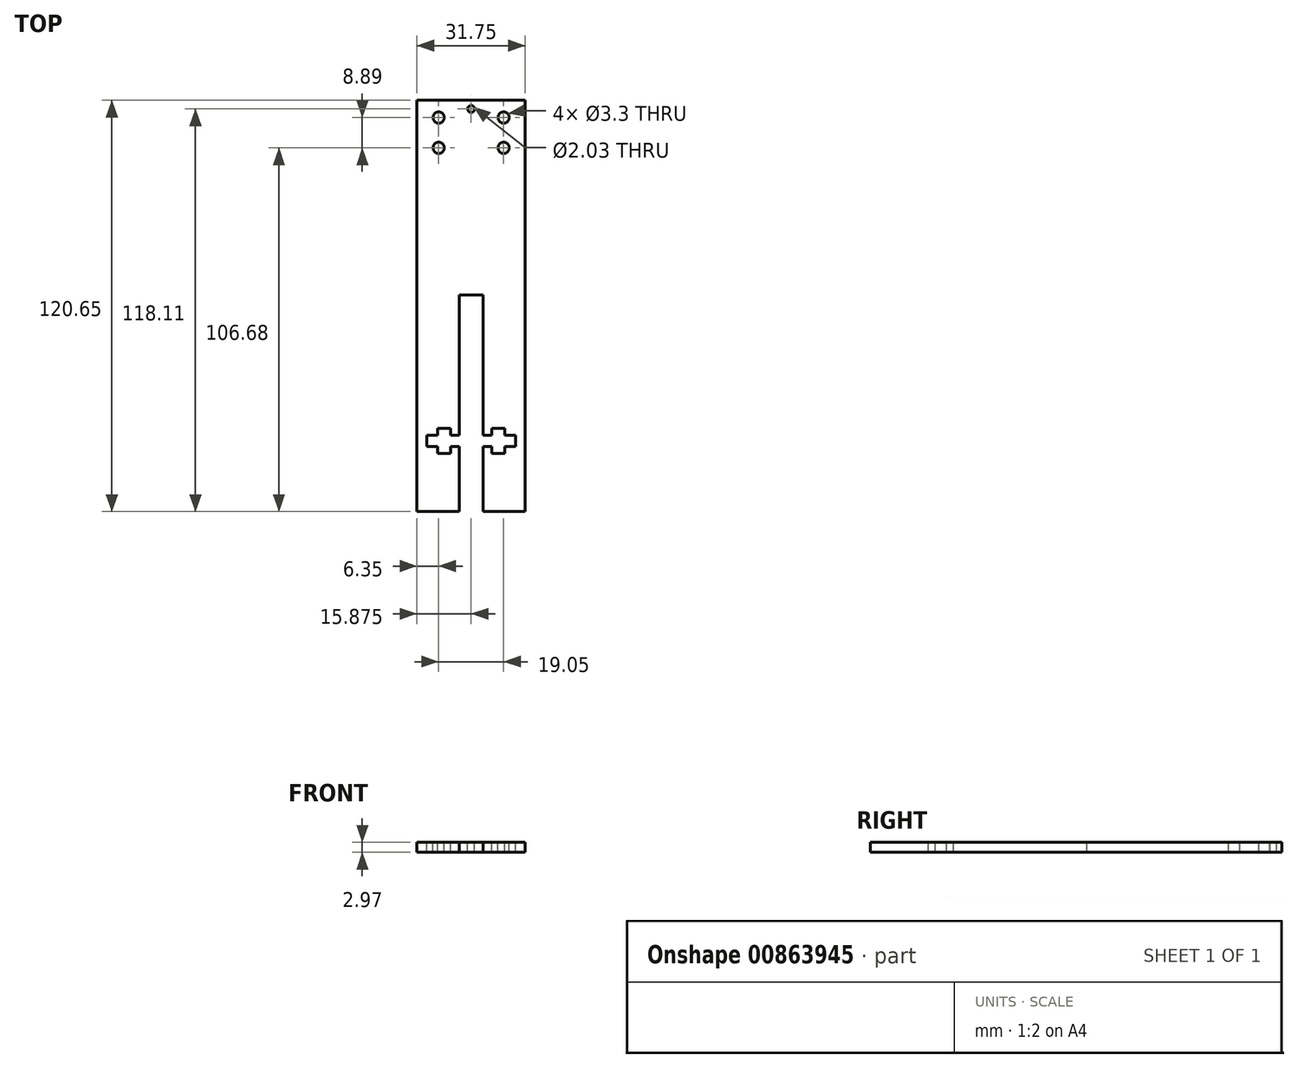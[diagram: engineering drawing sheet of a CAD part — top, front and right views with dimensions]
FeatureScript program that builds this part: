
annotation { "Feature Type Name" : "Feature", "Feature Type Description" : "" }
export const myFeature = defineFeature(function(context is Context, id is Id, definition is map)
    precondition{}
    {
        {
            var Q0;
            Q0=qCreatedBy(makeId("Top.planeOp"),FACE);
            var sketch = newSketch(context, id + "F0", { "sketchPlane" : qUnion([Q0])});
            skLineSegment(sketch, "E0.bottom", {"start": v(0, 0) * mm, "end": v(31.75, 0) * mm});
            skLineSegment(sketch, "E0.top", {"start": v(0, 120.65) * mm, "end": v(31.75, 120.65) * mm});
            skLineSegment(sketch, "E0.left", {"start": v(0, 0) * mm, "end": v(0, 120.65) * mm});
            skLineSegment(sketch, "E0.right", {"start": v(31.75, 0) * mm, "end": v(31.75, 120.65) * mm});
            skSolve(sketch);
        }
        {
            var Q0;
            Q0=makeQuery(id+"F0.imprint","IMPRINT",FACE,{"disambiguationData":[TD([[makeQuery(id+"F0.imprint","IMPRINT",EDGE,{"derivedFrom":sQuery(id+"F0.wireOp",EDGE,"E0.bottom")}),1.0]])]});
            extrude(context, id + "F1", {"entities" : qUnion([Q0]), "depth" : 2.97 * mm, "offsetDistance" : 25.4 * mm});
        }
        {
            var Q0;
            Q0=makeQuery(id+"F1.opExtrude","CAP_FACE",FACE,{"disambiguationData":[OSD([sQuery(id+"F0.wireOp",EDGE,"E0.bottom"),sQuery(id+"F0.wireOp",EDGE,"E0.top"),sQuery(id+"F0.wireOp",EDGE,"E0.left"),sQuery(id+"F0.wireOp",EDGE,"E0.right")])],"isStart":false});
            var sketch = newSketch(context, id + "F2", { "sketchPlane" : qUnion([Q0])});
            skCircle(sketch, "E1", {"center": v(6.35, 115.57) * mm, "radius": 1.65 * mm});
            skCircle(sketch, "E2", {"center": v(25.4, 115.57) * mm, "radius": 1.65 * mm});
            skCircle(sketch, "E3", {"center": v(6.35, 106.68) * mm, "radius": 1.65 * mm});
            skCircle(sketch, "E4", {"center": v(25.4, 106.68) * mm, "radius": 1.65 * mm});
            skCircle(sketch, "E5", {"center": v(15.87, 118.11) * mm, "radius": 1.02 * mm});
            skLineSegment(sketch, "E6.bottom", {"start": v(12.38, 0) * mm, "end": v(19.37, 0) * mm});
            skLineSegment(sketch, "E6.top", {"start": v(12.38, 63.5) * mm, "end": v(19.37, 63.5) * mm});
            skLineSegment(sketch, "E6.left", {"start": v(12.38, 0) * mm, "end": v(12.38, 63.5) * mm});
            skLineSegment(sketch, "E6.right", {"start": v(19.37, 0) * mm, "end": v(19.37, 63.5) * mm});
            skLineSegment(sketch, "E7.bottom", {"start": v(19.37, 22.35) * mm, "end": v(21.9, 22.35) * mm});
            skLineSegment(sketch, "E7.top", {"start": v(19.37, 19.05) * mm, "end": v(21.9, 19.05) * mm});
            skLineSegment(sketch, "E7.left", {"start": v(19.37, 22.35) * mm, "end": v(19.37, 19.05) * mm});
            skLineSegment(sketch, "E7.right", {"start": v(21.9, 22.35) * mm, "end": v(21.9, 19.05) * mm});
            skLineSegment(sketch, "E8.bottom", {"start": v(21.9, 24.38) * mm, "end": v(25.72, 24.38) * mm});
            skLineSegment(sketch, "E8.top", {"start": v(21.9, 17.02) * mm, "end": v(25.72, 17.02) * mm});
            skLineSegment(sketch, "E8.left", {"start": v(21.9, 24.38) * mm, "end": v(21.9, 17.02) * mm});
            skLineSegment(sketch, "E8.right", {"start": v(25.72, 24.38) * mm, "end": v(25.72, 17.02) * mm});
            skLineSegment(sketch, "E9.bottom", {"start": v(25.72, 22.35) * mm, "end": v(28.9, 22.35) * mm});
            skLineSegment(sketch, "E9.top", {"start": v(25.72, 19.05) * mm, "end": v(28.9, 19.05) * mm});
            skLineSegment(sketch, "E9.left", {"start": v(25.72, 22.35) * mm, "end": v(25.72, 19.05) * mm});
            skLineSegment(sketch, "E9.right", {"start": v(28.9, 22.35) * mm, "end": v(28.9, 19.05) * mm});
            skLineSegment(sketch, "E10.bottom", {"start": v(12.38, 19.05) * mm, "end": v(9.84, 19.05) * mm});
            skLineSegment(sketch, "E10.top", {"start": v(12.38, 22.35) * mm, "end": v(9.84, 22.35) * mm});
            skLineSegment(sketch, "E10.right", {"start": v(9.84, 19.05) * mm, "end": v(9.84, 22.35) * mm});
            skLineSegment(sketch, "E11.bottom", {"start": v(9.84, 17.02) * mm, "end": v(6.03, 17.02) * mm});
            skLineSegment(sketch, "E11.top", {"start": v(9.84, 24.38) * mm, "end": v(6.03, 24.38) * mm});
            skLineSegment(sketch, "E11.left", {"start": v(9.84, 17.02) * mm, "end": v(9.84, 24.38) * mm});
            skLineSegment(sketch, "E11.right", {"start": v(6.03, 17.02) * mm, "end": v(6.03, 24.38) * mm});
            skLineSegment(sketch, "E12.bottom", {"start": v(6.03, 19.05) * mm, "end": v(2.86, 19.05) * mm});
            skLineSegment(sketch, "E12.top", {"start": v(6.03, 22.35) * mm, "end": v(2.86, 22.35) * mm});
            skLineSegment(sketch, "E12.left", {"start": v(6.03, 19.05) * mm, "end": v(6.03, 22.35) * mm});
            skLineSegment(sketch, "E12.right", {"start": v(2.86, 19.05) * mm, "end": v(2.86, 22.35) * mm});
            skSolve(sketch);
        }
        {
            var Q0;
            Q0=makeQuery(id+"F2.imprint","IMPRINT",FACE,{"disambiguationData":[TD([[makeQuery(id+"F2.imprint","IMPRINT",EDGE,{"derivedFrom":sQuery(id+"F2.wireOp",EDGE,"E1")}),1.0]])]});
            var Q1;
            Q1=makeQuery(id+"F2.imprint","IMPRINT",FACE,{"disambiguationData":[TD([[makeQuery(id+"F2.imprint","IMPRINT",EDGE,{"derivedFrom":sQuery(id+"F2.wireOp",EDGE,"E2")}),1.0]])]});
            var Q2;
            Q2=makeQuery(id+"F2.imprint","IMPRINT",FACE,{"disambiguationData":[TD([[makeQuery(id+"F2.imprint","IMPRINT",EDGE,{"derivedFrom":sQuery(id+"F2.wireOp",EDGE,"E4")}),1.0]])]});
            var Q3;
            Q3=makeQuery(id+"F2.imprint","IMPRINT",FACE,{"disambiguationData":[TD([[makeQuery(id+"F2.imprint","IMPRINT",EDGE,{"derivedFrom":sQuery(id+"F2.wireOp",EDGE,"E3")}),1.0]])]});
            var Q4;
            Q4=makeQuery(id+"F2.imprint","IMPRINT",FACE,{"disambiguationData":[TD([[makeQuery(id+"F2.imprint","IMPRINT",EDGE,{"derivedFrom":sQuery(id+"F2.wireOp",EDGE,"E5")}),1.0]])]});
            var Q5;
            {var subQ3=sQuery(id+"F2.wireOp",EDGE,"E6.bottom");Q5=makeQuery(id+"F2.imprint","IMPRINT",FACE,{"disambiguationData":[TD([[makeQuery(id+"F2.imprint","IMPRINT",EDGE,{"derivedFrom":subQ3}),1.0]])]});}
            var Q6;
            {var subQ3=sQuery(id+"F2.wireOp",EDGE,"E8.bottom");Q6=makeQuery(id+"F2.imprint","IMPRINT",FACE,{"disambiguationData":[TD([[makeQuery(id+"F2.imprint","IMPRINT",EDGE,{"derivedFrom":subQ3}),-1.0]])]});}
            var Q7;
            Q7=makeQuery(id+"F2.imprint","IMPRINT",FACE,{"disambiguationData":[TD([[makeQuery(id+"F2.imprint","IMPRINT",EDGE,{"derivedFrom":sQuery(id+"F2.wireOp",EDGE,"E9.bottom")}),-1.0]])]});
            var Q8;
            {var subQ0=sQuery(id+"F2.wireOp",EDGE,"E7.bottom");Q8=makeQuery(id+"F2.imprint","IMPRINT",FACE,{"disambiguationData":[TD([[makeQuery(id+"F2.imprint","IMPRINT",EDGE,{"derivedFrom":subQ0}),-1.0]])]});}
            var Q9;
            {var subQ0=sQuery(id+"F2.wireOp",EDGE,"E10.bottom");Q9=makeQuery(id+"F2.imprint","IMPRINT",FACE,{"disambiguationData":[TD([[makeQuery(id+"F2.imprint","IMPRINT",EDGE,{"derivedFrom":subQ0}),-1.0]])]});}
            var Q10;
            {var subQ3=sQuery(id+"F2.wireOp",EDGE,"E11.bottom");Q10=makeQuery(id+"F2.imprint","IMPRINT",FACE,{"disambiguationData":[TD([[makeQuery(id+"F2.imprint","IMPRINT",EDGE,{"derivedFrom":subQ3}),-1.0]])]});}
            var Q11;
            Q11=makeQuery(id+"F2.imprint","IMPRINT",FACE,{"disambiguationData":[TD([[makeQuery(id+"F2.imprint","IMPRINT",EDGE,{"derivedFrom":sQuery(id+"F2.wireOp",EDGE,"E12.bottom")}),-1.0]])]});
            var Q12;
            Q12=sQuery(id+"F2.wireOp",EDGE,"E4");
            var Q13;
            Q13=sQuery(id+"F2.wireOp",EDGE,"E3");
            var Q14;
            Q14=sQuery(id+"F2.wireOp",EDGE,"E1");
            var Q15;
            Q15=sQuery(id+"F2.wireOp",EDGE,"E2");
            extrude(context, id + "F3", {"entities" : qUnion([Q0, Q1, Q2, Q3, Q4, Q5, Q6, Q7, Q8, Q9, Q10, Q11]), "operationType" : NewBodyOperationType.REMOVE, "surfaceEntities" : qUnion([Q12, Q13, Q14, Q15]), "oppositeDirection" : true, "depth" : 25.4 * mm, "offsetDistance" : 25.4 * mm});
        }
    });
